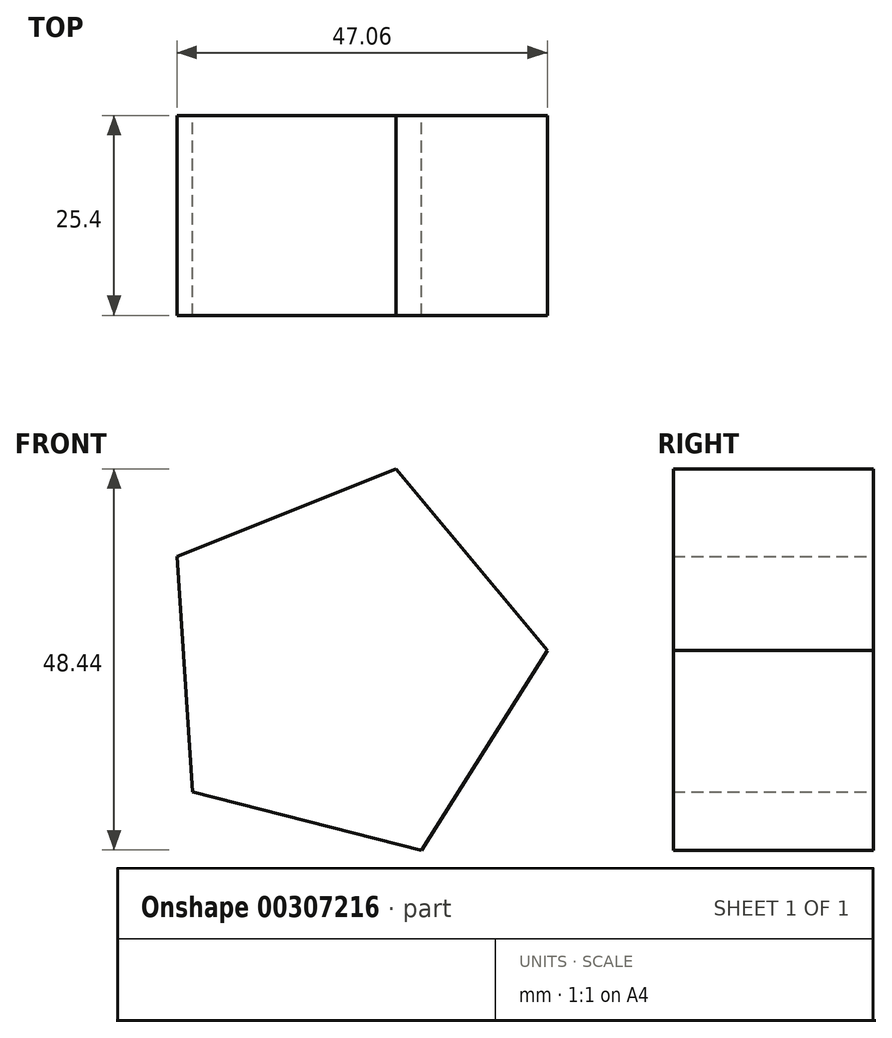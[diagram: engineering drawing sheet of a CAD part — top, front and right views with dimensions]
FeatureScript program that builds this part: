
annotation { "Feature Type Name" : "Feature", "Feature Type Description" : "" }
export const myFeature = defineFeature(function(context is Context, id is Id, definition is map)
    precondition{}
    {
        {
            var Q0;
            Q0=qCreatedBy(makeId("Front.planeOp"),FACE);
            var sketch = newSketch(context, id + "F0", { "sketchPlane" : qUnion([Q0])});
            skCircle(sketch, "E0.cCircle", {"center": v(-60.64, 50.73) * mm, "radius": 25.52 * mm, "construction": true});
            skLineSegment(sketch, "E0.0", {"start": v(-82.23, 64.33) * mm, "end": v(-54.37, 75.47) * mm});
            skLineSegment(sketch, "E0.1", {"start": v(-54.37, 75.47) * mm, "end": v(-35.17, 52.41) * mm});
            skLineSegment(sketch, "E0.2", {"start": v(-35.17, 52.41) * mm, "end": v(-51.16, 27.03) * mm});
            skLineSegment(sketch, "E0.3", {"start": v(-51.16, 27.03) * mm, "end": v(-80.25, 34.4) * mm});
            skLineSegment(sketch, "E0.4", {"start": v(-80.25, 34.4) * mm, "end": v(-82.23, 64.33) * mm});
            skSolve(sketch);
        }
        {
            var Q0;
            Q0=makeQuery(id+"F0.imprint","IMPRINT",FACE,{"disambiguationData":[TD([[makeQuery(id+"F0.imprint","IMPRINT",EDGE,{"derivedFrom":sQuery(id+"F0.wireOp",EDGE,"E0.0")}),-1.0]])]});
            extrude(context, id + "F1", {"entities" : qUnion([Q0]), "depth" : 25.4 * mm});
        }
    });
